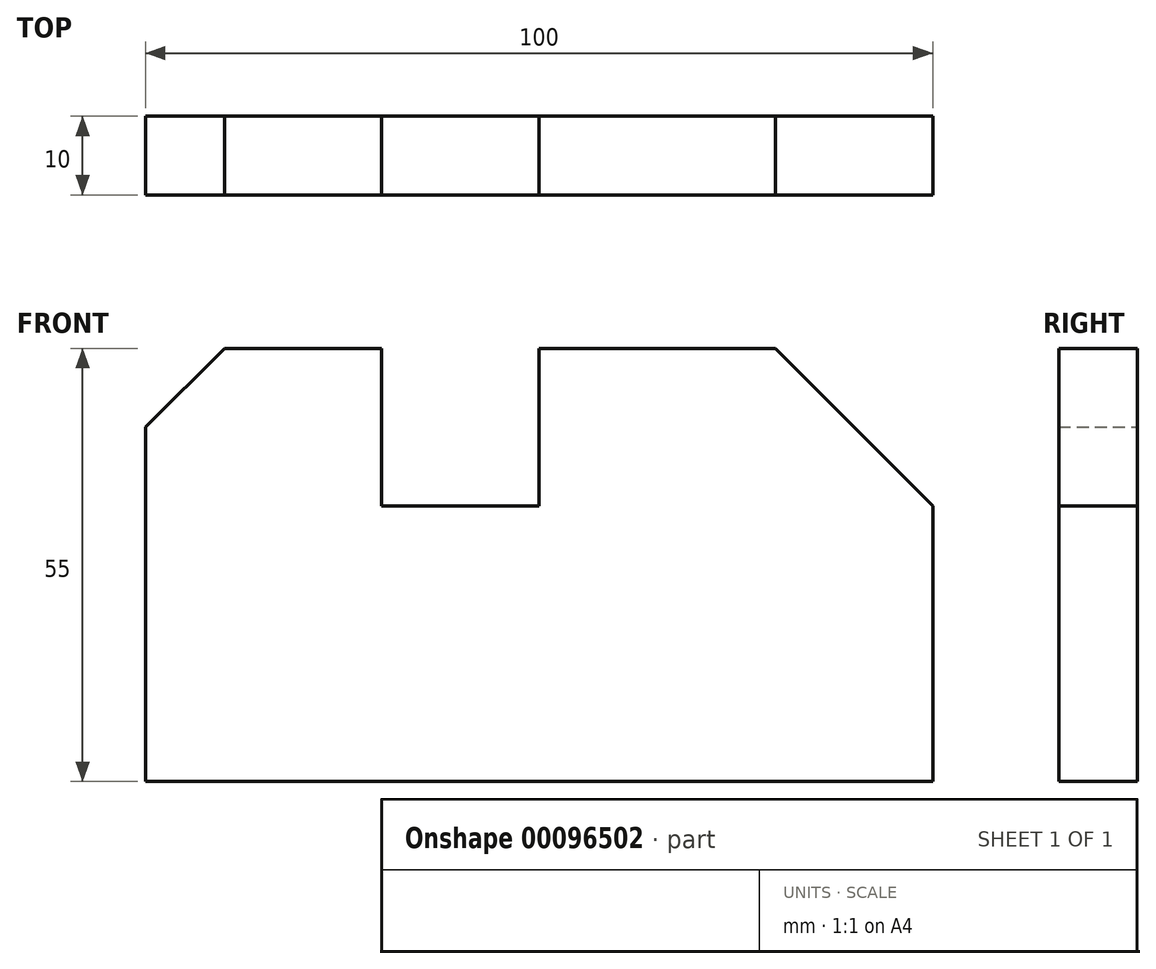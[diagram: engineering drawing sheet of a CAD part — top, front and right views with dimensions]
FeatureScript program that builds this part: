
annotation { "Feature Type Name" : "Feature", "Feature Type Description" : "" }
export const myFeature = defineFeature(function(context is Context, id is Id, definition is map)
    precondition{}
    {
        {
            var Q0;
            Q0=qCreatedBy(makeId("Front.planeOp"),FACE);
            var sketch = newSketch(context, id + "F0", { "sketchPlane" : qUnion([Q0])});
            skLineSegment(sketch, "E0", {"start": v(0, 0) * mm, "end": v(100, 0) * mm});
            skLineSegment(sketch, "E1", {"start": v(100, 0) * mm, "end": v(100, 35) * mm});
            skLineSegment(sketch, "E2", {"start": v(100, 35) * mm, "end": v(80, 55) * mm});
            skLineSegment(sketch, "E3", {"start": v(80, 55) * mm, "end": v(50, 55) * mm});
            skLineSegment(sketch, "E4", {"start": v(50, 55) * mm, "end": v(50, 35) * mm});
            skLineSegment(sketch, "E5", {"start": v(50, 35) * mm, "end": v(30, 35) * mm});
            skLineSegment(sketch, "E6", {"start": v(30, 35) * mm, "end": v(30, 55) * mm});
            skLineSegment(sketch, "E7", {"start": v(30, 55) * mm, "end": v(10, 55) * mm});
            skLineSegment(sketch, "E8", {"start": v(10, 55) * mm, "end": v(0, 45) * mm});
            skLineSegment(sketch, "E9", {"start": v(0, 45) * mm, "end": v(0, 0) * mm});
            skSolve(sketch);
        }
        {
            var Q0;
            Q0 = qSketchRegion(id + "F0", true);
            extrude(context, id + "F1", {"entities" : qUnion([Q0]), "depth" : 10 * mm});
        }
    });
